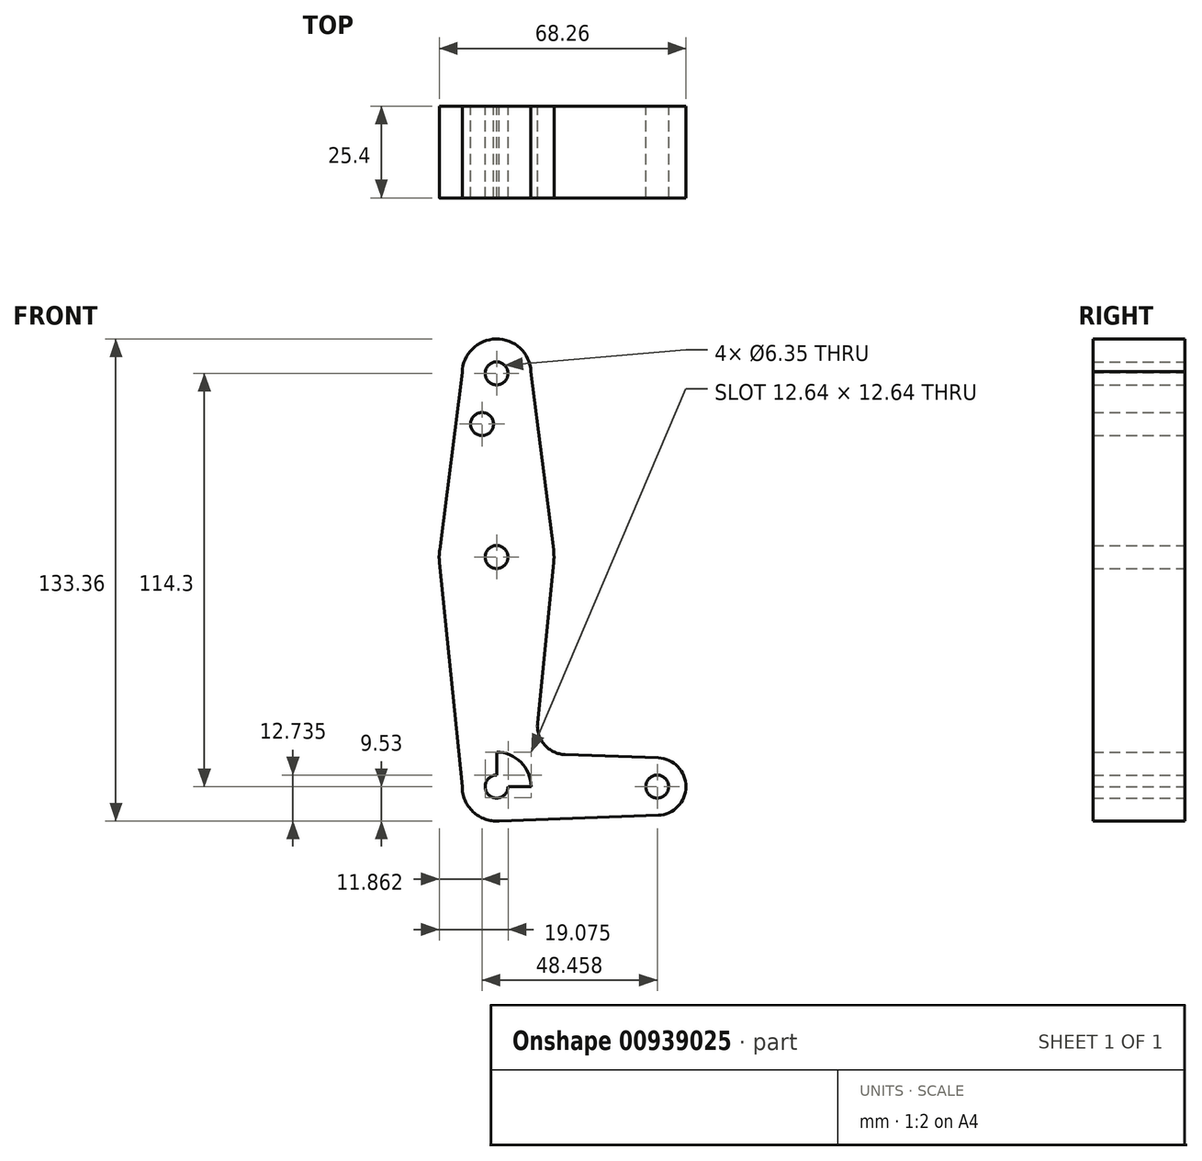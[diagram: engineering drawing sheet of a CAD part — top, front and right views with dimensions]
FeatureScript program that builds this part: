
annotation { "Feature Type Name" : "Feature", "Feature Type Description" : "" }
export const myFeature = defineFeature(function(context is Context, id is Id, definition is map)
    precondition{}
    {
        {
            var Q0;
            Q0=qCreatedBy(makeId("Front.planeOp"),FACE);
            var sketch = newSketch(context, id + "F0", { "sketchPlane" : qUnion([Q0])});
            skLineSegment(sketch, "E0", {"start": v(0, 0) * mm, "end": v(44.45, 0) * mm});
            skCircle(sketch, "E1", {"center": v(44.45, 0) * mm, "radius": 7.94 * mm});
            skCircle(sketch, "E2", {"center": v(0, 0) * mm, "radius": 9.53 * mm});
            skCircle(sketch, "E3", {"center": v(0, 114.3) * mm, "radius": 9.53 * mm});
            skCircle(sketch, "E4", {"center": v(0, 63.5) * mm, "radius": 15.88 * mm});
            skLineSegment(sketch, "E5", {"start": v(0, 63.5) * mm, "end": v(0, 0) * mm});
            skLineSegment(sketch, "E6", {"start": v(0, 114.3) * mm, "end": v(0, 0) * mm});
            skLineSegment(sketch, "E7", {"start": v(0, -9.53) * mm, "end": v(44.73, -7.93) * mm});
            skLineSegment(sketch, "E8", {"start": v(18.97, 8.85) * mm, "end": v(44.73, 7.93) * mm});
            skLineSegment(sketch, "E9", {"start": v(-9.52, 0) * mm, "end": v(-15.8, 61.9) * mm});
            skLineSegment(sketch, "E10", {"start": v(15.8, 61.9) * mm, "end": v(11.34, 17.59) * mm});
            skLineSegment(sketch, "E11", {"start": v(-9.52, 114.52) * mm, "end": v(-15.75, 65.5) * mm});
            skCircle(sketch, "E12", {"center": v(0, 114.3) * mm, "radius": 3.18 * mm});
            skCircle(sketch, "E13", {"center": v(0, 63.5) * mm, "radius": 3.18 * mm});
            skCircle(sketch, "E14", {"center": v(-4, 100.27) * mm, "radius": 3.17 * mm});
            skCircle(sketch, "E15", {"center": v(0, 0) * mm, "radius": 3.18 * mm});
            skCircle(sketch, "E16", {"center": v(44.45, 0) * mm, "radius": 3.18 * mm});
            skLineSegment(sketch, "E17", {"start": v(9.51, 114.82) * mm, "end": v(15.75, 65.5) * mm});
            skPoint(sketch, "E18.newPointA", {"position": v(9.57, 0) * mm});
            skArc(sketch, "E18.filletArc", {"start": v(11.34, 17.59) * mm, "mid": v(13.26, 11.57) * mm, "end": v(18.97, 8.85) * mm});
            skSolve(sketch);
        }
        {
            var Q0;
            Q0 = qSketchRegion(id + "F0", true);
            extrude(context, id + "F1", {"entities" : qUnion([Q0]), "depth" : 25.4 * mm, "offsetDistance" : 25.4 * mm});
        }
    });
